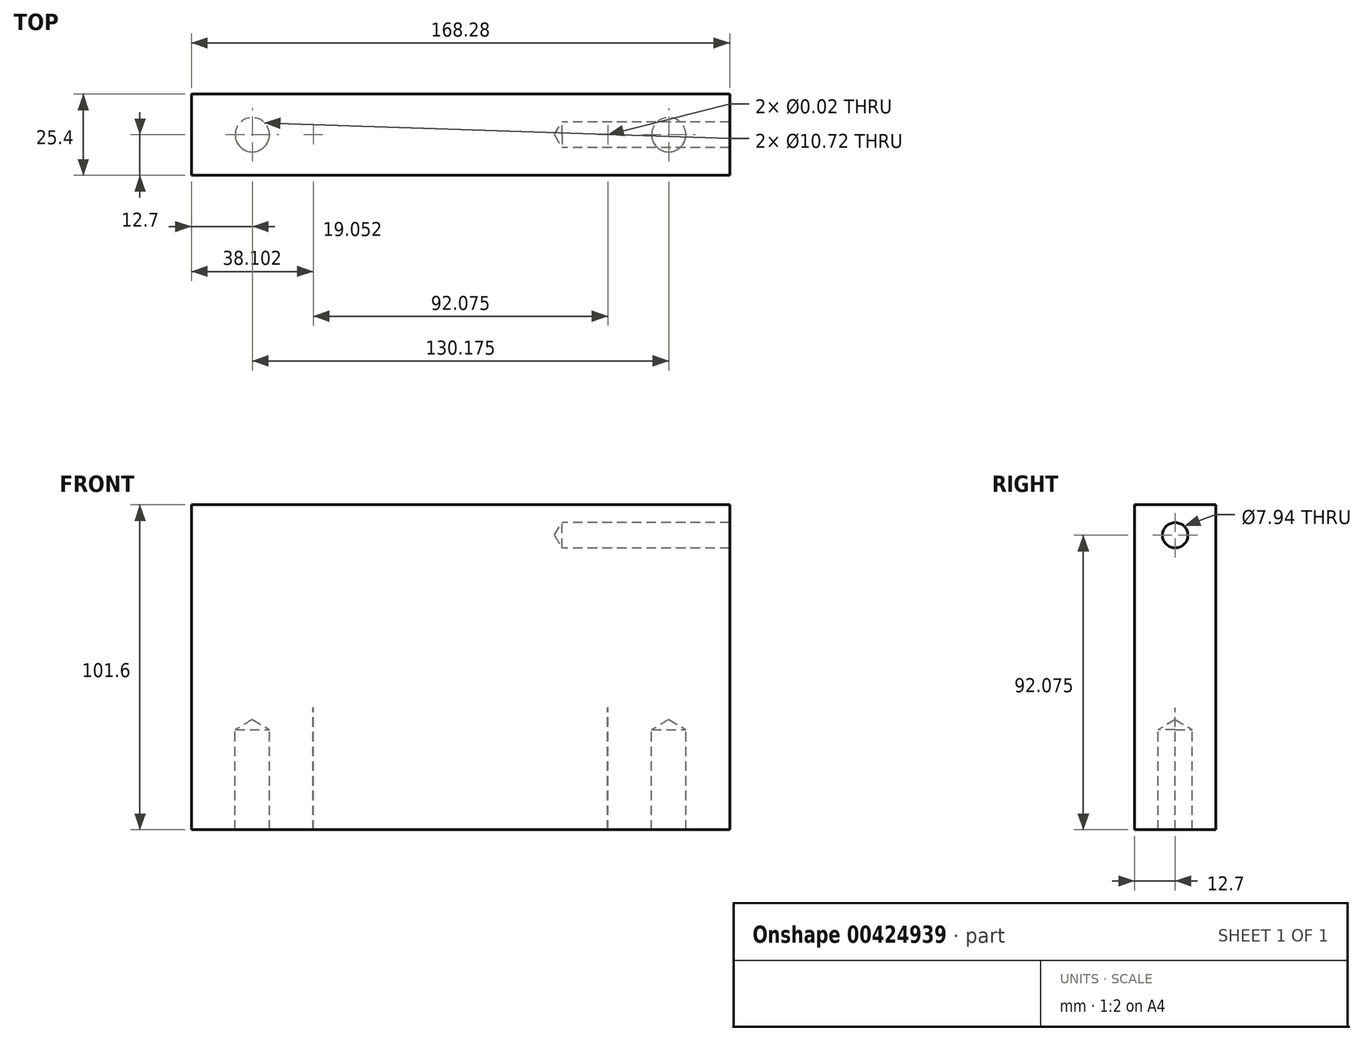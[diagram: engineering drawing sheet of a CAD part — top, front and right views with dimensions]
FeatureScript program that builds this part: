
annotation { "Feature Type Name" : "Feature", "Feature Type Description" : "" }
export const myFeature = defineFeature(function(context is Context, id is Id, definition is map)
    precondition{}
    {
        {
            var Q0;
            Q0=qCreatedBy(makeId("Front.planeOp"),FACE);
            var sketch = newSketch(context, id + "F0", { "sketchPlane" : qUnion([Q0])});
            skLineSegment(sketch, "E0.bottom", {"start": v(84.14, -50.8) * mm, "end": v(-84.14, -50.8) * mm});
            skLineSegment(sketch, "E0.top", {"start": v(84.14, 50.8) * mm, "end": v(-84.14, 50.8) * mm});
            skLineSegment(sketch, "E0.left", {"start": v(84.14, -50.8) * mm, "end": v(84.14, 50.8) * mm});
            skLineSegment(sketch, "E0.right", {"start": v(-84.14, -50.8) * mm, "end": v(-84.14, 50.8) * mm});
            skPoint(sketch, "E0.middle", {"position": v(0, 0) * mm});
            skSolve(sketch);
        }
        {
            var Q0;
            Q0=makeQuery(id+"F0.imprint","IMPRINT",FACE,{"disambiguationData":[TD([[makeQuery(id+"F0.imprint","IMPRINT",EDGE,{"derivedFrom":sQuery(id+"F0.wireOp",EDGE,"E0.bottom")}),-1.0]])]});
            extrude(context, id + "F1", {"entities" : qUnion([Q0]), "depth" : 25.4 * mm, "symmetric" : true});
        }
        {
            var Q0;
            Q0=makeQuery(id+"F1.opExtrude","SWEPT_FACE",FACE,{"disambiguationData":[OSD([sQuery(id+"F0.wireOp",EDGE,"E0.bottom")])]});
            var sketch = newSketch(context, id + "F2", { "sketchPlane" : qUnion([Q0])});
            skLineSegment(sketch, "E1", {"start": v(84.14, 0) * mm, "end": v(-84.14, 0) * mm, "construction": true});
            skPoint(sketch, "E2", {"position": v(65.09, 0) * mm});
            skPoint(sketch, "E3", {"position": v(46.04, 0) * mm});
            skPoint(sketch, "E4", {"position": v(-46.04, 0) * mm});
            skPoint(sketch, "E5", {"position": v(-65.09, 0) * mm});
            skSolve(sketch);
        }
        {
            var Q0;
            Q0=sQuery(id+"F2.wireOp",VERTEX,"E3");
            var Q1;
            Q1=sQuery(id+"F2.wireOp",VERTEX,"E4");
            var Q2;
            Q2=makeQuery(id+"F1.opExtrude","SWEPT_BODY",BODY,{"disambiguationData":[OSD([sQuery(id+"F0.wireOp",EDGE,"E0.bottom"),sQuery(id+"F0.wireOp",EDGE,"E0.top"),sQuery(id+"F0.wireOp",EDGE,"E0.left"),sQuery(id+"F0.wireOp",EDGE,"E0.right")])]});
            hole(context, id + "F3", {"style" : HoleStyle.SIMPLE, "endStyle" : HoleEndStyle.BLIND, "standardTappedOrClearance" : lookupTablePath({ "standard" : "ANSI", "size" : "1/2 (0.5)", "type" : "Drilled" }), "standardBlindInLast" : lookupTablePath({ "standard" : "ANSI", "size" : "1/2", "type" : "Drilled" }), "holeDiameter" : 1 / 50.8 * mm, "holeDepth" : 38.1 * mm, "isTappedThrough" : true, "tappedDepth" : 5.08 * mm, "tapClearance" : 3, "locations" : qUnion([Q0, Q1]), "scope" : qUnion([Q2]), "startStyle" : HoleStartStyle.SKETCH});
        }
        {
            var Q0;
            Q0=sQuery(id+"F2.wireOp",VERTEX,"E2");
            var Q1;
            Q1=sQuery(id+"F2.wireOp",VERTEX,"E5");
            var Q2;
            Q2=makeQuery(id+"F1.opExtrude","SWEPT_BODY",BODY,{"disambiguationData":[OSD([sQuery(id+"F0.wireOp",EDGE,"E0.bottom"),sQuery(id+"F0.wireOp",EDGE,"E0.top"),sQuery(id+"F0.wireOp",EDGE,"E0.left"),sQuery(id+"F0.wireOp",EDGE,"E0.right")])]});
            hole(context, id + "F4", {"style" : HoleStyle.SIMPLE, "endStyle" : HoleEndStyle.BLIND, "standardTappedOrClearance" : lookupTablePath({ "standard" : "ANSI", "engagement" : "75%", "pitch" : "13 tpi", "size" : "1/2", "type" : "Tapped" }), "standardBlindInLast" : lookupTablePath({ "standard" : "ANSI", "engagement" : "75%", "pitch" : "13 tpi", "size" : "1/2", "type" : "Tapped" }), "holeDiameter" : 10.72 * mm, "showTappedDepth" : true, "holeDepth" : 31.26 * mm, "isTappedThrough" : true, "tappedDepth" : 25.4 * mm, "tapClearance" : 3, "locations" : qUnion([Q0, Q1]), "scope" : qUnion([Q2]), "majorDiameter" : 12.7 * mm, "startStyle" : HoleStartStyle.SKETCH});
        }
        {
            var Q0;
            Q0=makeQuery(id+"F1.opExtrude","SWEPT_FACE",FACE,{"disambiguationData":[OSD([sQuery(id+"F0.wireOp",EDGE,"E0.left")])]});
            var sketch = newSketch(context, id + "F5", { "sketchPlane" : qUnion([Q0])});
            skLineSegment(sketch, "E6", {"start": v(0, 50.8) * mm, "end": v(0, -50.8) * mm, "construction": true});
            skPoint(sketch, "E7", {"position": v(0, 41.28) * mm});
            skSolve(sketch);
        }
        {
            var Q0;
            Q0=sQuery(id+"F5.wireOp",VERTEX,"E7");
            var Q1;
            Q1=makeQuery(id+"F1.opExtrude","SWEPT_BODY",BODY,{"disambiguationData":[OSD([sQuery(id+"F0.wireOp",EDGE,"E0.bottom"),sQuery(id+"F0.wireOp",EDGE,"E0.top"),sQuery(id+"F0.wireOp",EDGE,"E0.left"),sQuery(id+"F0.wireOp",EDGE,"E0.right")])]});
            hole(context, id + "F6", {"style" : HoleStyle.SIMPLE, "endStyle" : HoleEndStyle.BLIND, "standardTappedOrClearance" : lookupTablePath({ "standard" : "ANSI", "size" : "1/2 (0.5)", "type" : "Drilled" }), "standardBlindInLast" : lookupTablePath({ "standard" : "ANSI", "size" : "1/2", "type" : "Drilled" }), "holeDiameter" : 1 / 50.8 * mm, "holeDepth" : 25.4 * mm, "isTappedThrough" : true, "tappedDepth" : 25.4 * mm, "tapClearance" : 3, "locations" : qUnion([Q0]), "scope" : qUnion([Q1]), "startStyle" : HoleStartStyle.SKETCH});
        }
        {
            var Q0;
            {var subQ0=sQuery(id+"F0.wireOp",EDGE,"E0.left");Q0=makeQuery(id+"F5.imprint","IMPRINT",FACE,{"disambiguationData":[TD([[makeQuery(id+"F5.imprint","IMPRINT",EDGE,{"derivedFrom":makeQuery(id+"F1.opExtrude","CAP_EDGE",EDGE,{"disambiguationData":[OSD([subQ0])],"isStart":true})}),1.0]])]});}
            cPlane(context, id + "F7", {"entities" : qUnion([Q0]), "cplaneType" : CPlaneType.OFFSET, "offset" : 25.4 * mm, "oppositeDirection" : true, "width" : 152.4 * mm, "height" : 152.4 * mm});
        }
        {
            var Q0;
            Q0=qCreatedBy(id+"F7.planeOp",FACE);
            var sketch = newSketch(context, id + "F8", { "sketchPlane" : qUnion([Q0])});
            skPoint(sketch, "E8.0", {"position": v(0, 41.28) * mm});
            skSolve(sketch);
        }
        {
            var Q0;
            Q0=sQuery(id+"F8.wireOp",VERTEX,"E8.0");
            var Q1;
            Q1=makeQuery(id+"F1.opExtrude","SWEPT_BODY",BODY,{"disambiguationData":[OSD([sQuery(id+"F0.wireOp",EDGE,"E0.bottom"),sQuery(id+"F0.wireOp",EDGE,"E0.top"),sQuery(id+"F0.wireOp",EDGE,"E0.left"),sQuery(id+"F0.wireOp",EDGE,"E0.right")])]});
            hole(context, id + "F9", {"style" : HoleStyle.SIMPLE, "endStyle" : HoleEndStyle.BLIND, "standardTappedOrClearance" : lookupTablePath({ "standard" : "ANSI", "engagement" : "75%", "pitch" : "16 tpi", "size" : "3/8", "type" : "Tapped" }), "standardBlindInLast" : lookupTablePath({ "standard" : "ANSI", "engagement" : "75%", "pitch" : "16 tpi", "size" : "3/8", "type" : "Tapped" }), "holeDiameter" : 7.94 * mm, "showTappedDepth" : true, "holeDepth" : 27 * mm, "isTappedThrough" : true, "tappedDepth" : 22.24 * mm, "tapClearance" : 3, "locations" : qUnion([Q0]), "scope" : qUnion([Q1]), "majorDiameter" : 9.53 * mm, "startStyle" : HoleStartStyle.SKETCH});
        }
    });
